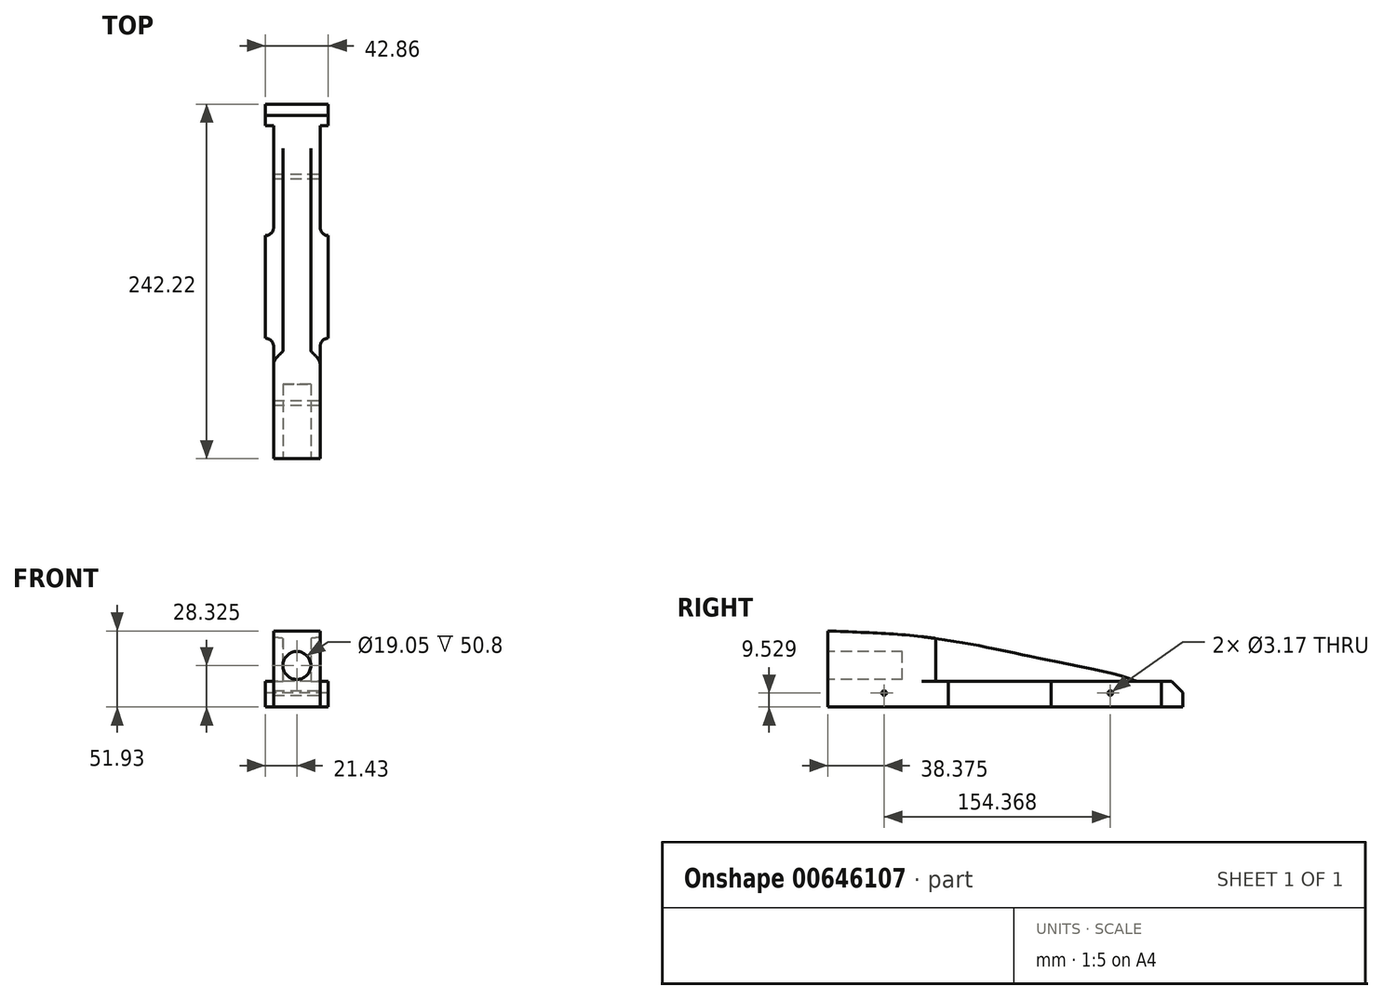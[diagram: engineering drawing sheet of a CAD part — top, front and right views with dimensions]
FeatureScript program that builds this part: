
annotation { "Feature Type Name" : "Feature", "Feature Type Description" : "" }
export const myFeature = defineFeature(function(context is Context, id is Id, definition is map)
    precondition{}
    {
        {
            var Q0;
            Q0=qCreatedBy(makeId("Right.planeOp"),FACE);
            var sketch = newSketch(context, id + "F0", { "sketchPlane" : qUnion([Q0])});
            skLineSegment(sketch, "E0", {"start": v(-152.4, 0) * mm, "end": v(152.4, 0) * mm});
            skLineSegment(sketch, "E1", {"start": v(-152.4, 0) * mm, "end": v(-152.4, 69.85) * mm});
            skLineSegment(sketch, "E2", {"start": v(152.4, 0) * mm, "end": v(152.4, 19.05) * mm});
            skLineSegment(sketch, "E3", {"start": v(152.4, 19.05) * mm, "end": v(-152.4, 69.85) * mm});
            skPoint(sketch, "E4.endSnap0", {"position": v(-152.4, 34.93) * mm});
            skLineSegment(sketch, "E5.0", {"start": v(-95.25, 50.8) * mm, "end": v(-152.4, 50.8) * mm, "construction": true});
            skLineSegment(sketch, "E5.1", {"start": v(-95.25, 50.8) * mm, "end": v(-95.25, 19.05) * mm, "construction": true});
            skLineSegment(sketch, "E5.2", {"start": v(-95.25, 19.05) * mm, "end": v(-152.4, 19.05) * mm, "construction": true});
            skSolve(sketch);
        }
        {
            var Q0;
            Q0=makeQuery(id+"F0.imprint","IMPRINT",FACE,{"disambiguationData":[TD([[makeQuery(id+"F0.imprint","IMPRINT",EDGE,{"derivedFrom":sQuery(id+"F0.wireOp",EDGE,"E0")}),1.0]])]});
            extrude(context, id + "F1", {"entities" : qUnion([Q0]), "depth" : 42.86 * mm, "symmetric" : true});
        }
        {
            var Q0;
            Q0=makeQuery(id+"F1.opExtrude","SWEPT_FACE",FACE,{"disambiguationData":[OSD([sQuery(id+"F0.wireOp",EDGE,"E1")])]});
            var sketch = newSketch(context, id + "F2", { "sketchPlane" : qUnion([Q0])});
            skLineSegment(sketch, "E6", {"start": v(21.43, 34.93) * mm, "end": v(0, 34.93) * mm, "construction": true});
            skCircle(sketch, "E7", {"center": v(0, 34.93) * mm, "radius": 9.53 * mm});
            skSolve(sketch);
        }
        {
            var Q0;
            Q0=makeQuery(id+"F2.imprint","IMPRINT",FACE,{"disambiguationData":[TD([[makeQuery(id+"F2.imprint","IMPRINT",EDGE,{"derivedFrom":sQuery(id+"F2.wireOp",EDGE,"E7")}),1.0]])]});
            var Q1;
            Q1=sQuery(id+"F2.wireOp",EDGE,"E7");
            extrude(context, id + "F3", {"entities" : qUnion([Q0]), "operationType" : NewBodyOperationType.REMOVE, "surfaceEntities" : qUnion([Q1]), "oppositeDirection" : true, "depth" : 50.8 * mm});
        }
        {
            var Q0;
            Q0=makeQuery(id+"F1.opExtrude","CAP_FACE",FACE,{"disambiguationData":[OSD([sQuery(id+"F0.wireOp",EDGE,"E0"),sQuery(id+"F0.wireOp",EDGE,"E1"),sQuery(id+"F0.wireOp",EDGE,"E2"),sQuery(id+"F0.wireOp",EDGE,"E3")])],"isStart":false});
            var sketch = newSketch(context, id + "F4", { "sketchPlane" : qUnion([Q0])});
            skLineSegment(sketch, "E8", {"start": v(-152.4, 34.93) * mm, "end": v(-152.4, 44.45) * mm, "construction": true});
            skLineSegment(sketch, "E9.0", {"start": v(-95.25, 19.05) * mm, "end": v(-152.4, 19.05) * mm, "construction": true});
            skLineSegment(sketch, "E9.1", {"start": v(-95.25, 50.8) * mm, "end": v(-95.25, 19.05) * mm, "construction": true});
            skLineSegment(sketch, "E9.2", {"start": v(-152.4, 50.8) * mm, "end": v(-95.25, 50.8) * mm, "construction": true});
            skLineSegment(sketch, "E10", {"start": v(-152.4, 44.45) * mm, "end": v(-101.6, 44.45) * mm, "construction": true});
            skLineSegment(sketch, "E11", {"start": v(-101.6, 44.45) * mm, "end": v(-101.6, 25.4) * mm, "construction": true});
            skLineSegment(sketch, "E12", {"start": v(-101.6, 25.4) * mm, "end": v(-152.4, 25.4) * mm, "construction": true});
            skFitSpline(sketch, "E13", {"points": [v(-152.4, 58.53) * mm, v(-91.68, 54.96) * mm, v(-40.9, 46.73) * mm, v(0, 38.24) * mm, v(57.15, 24.13) * mm], "startDerivative": vector(228.74, -10.44) * mm, "endDerivative": vector(48.82, -45.78) * mm});
            skLineSegment(sketch, "E14", {"start": v(57.15, 24.13) * mm, "end": v(57.15, 24.13) * mm});
            skLineSegment(sketch, "E15", {"start": v(-152.4, 50.8) * mm, "end": v(-152.4, 58.53) * mm});
            skPoint(sketch, "E16", {"position": v(0, 44.45) * mm});
            skLineSegment(sketch, "E17", {"start": v(57.15, 24.13) * mm, "end": v(166.37, 24.13) * mm});
            skLineSegment(sketch, "E18", {"start": v(166.37, 24.13) * mm, "end": v(-166.53, 95.56) * mm});
            skLineSegment(sketch, "E19", {"start": v(-166.53, 95.56) * mm, "end": v(-152.4, 58.53) * mm});
            skSolve(sketch);
        }
        {
            var Q0;
            Q0=makeQuery(id+"F1.opExtrude","SWEPT_FACE",FACE,{"disambiguationData":[OSD([sQuery(id+"F0.wireOp",EDGE,"E0")])]});
            var sketch = newSketch(context, id + "F5", { "sketchPlane" : qUnion([Q0])});
            skLineSegment(sketch, "E20", {"start": v(15.88, 152.4) * mm, "end": v(15.88, 95.25) * mm, "construction": true});
            skLineSegment(sketch, "E21", {"start": v(15.88, 95.25) * mm, "end": v(-15.87, 95.25) * mm, "construction": true});
            skLineSegment(sketch, "E22", {"start": v(-15.87, 95.25) * mm, "end": v(-15.87, 152.4) * mm, "construction": true});
            skLineSegment(sketch, "E23", {"start": v(0, 152.4) * mm, "end": v(-9.53, 152.4) * mm, "construction": true});
            skLineSegment(sketch, "E24", {"start": v(-9.53, 152.4) * mm, "end": v(-9.53, 101.6) * mm, "construction": true});
            skLineSegment(sketch, "E25", {"start": v(-9.52, 101.6) * mm, "end": v(9.53, 101.6) * mm, "construction": true});
            skLineSegment(sketch, "E26", {"start": v(9.53, 101.6) * mm, "end": v(9.53, 152.4) * mm, "construction": true});
            skLineSegment(sketch, "E27", {"start": v(15.88, 152.4) * mm, "end": v(15.88, 95.25) * mm});
            skLineSegment(sketch, "E28", {"start": v(-15.87, 95.25) * mm, "end": v(-15.87, 152.4) * mm});
            skLineSegment(sketch, "E29", {"start": v(15.88, 95.25) * mm, "end": v(15.88, 75.65) * mm});
            skLineSegment(sketch, "E30", {"start": v(-15.87, 95.25) * mm, "end": v(-15.87, 75.65) * mm});
            skLineSegment(sketch, "E31", {"start": v(-21.43, 70.1) * mm, "end": v(-21.43, 0) * mm});
            skLineSegment(sketch, "E32", {"start": v(21.43, 70.1) * mm, "end": v(21.43, 0) * mm});
            skLineSegment(sketch, "E33", {"start": v(21.43, 0) * mm, "end": v(21.43, -5.56) * mm});
            skArc(sketch, "E34", {"start": v(-21.43, 70.1) * mm, "mid": v(-17.5, 71.72) * mm, "end": v(-15.87, 75.65) * mm});
            skArc(sketch, "E35", {"start": v(15.88, 75.65) * mm, "mid": v(17.5, 71.72) * mm, "end": v(21.43, 70.1) * mm});
            skArc(sketch, "E36", {"start": v(21.43, 0) * mm, "mid": v(17.5, -1.63) * mm, "end": v(15.87, -5.56) * mm});
            skArc(sketch, "E37", {"start": v(-15.87, -5.56) * mm, "mid": v(-17.5, -1.63) * mm, "end": v(-21.43, 0) * mm});
            skLineSegment(sketch, "E38", {"start": v(-15.87, -5.56) * mm, "end": v(-15.87, -43.38) * mm});
            skLineSegment(sketch, "E39", {"start": v(15.87, -5.56) * mm, "end": v(15.87, -43.38) * mm});
            skLineSegment(sketch, "E40", {"start": v(15.87, -43.38) * mm, "end": v(15.87, -75.12) * mm});
            skLineSegment(sketch, "E41", {"start": v(-15.87, -43.38) * mm, "end": v(-15.87, -75.12) * mm});
            skLineSegment(sketch, "E42", {"start": v(-15.87, -75.12) * mm, "end": v(-21.43, -75.12) * mm});
            skLineSegment(sketch, "E43", {"start": v(-21.43, -75.12) * mm, "end": v(-21.43, -89.82) * mm});
            skLineSegment(sketch, "E44", {"start": v(-21.43, -89.82) * mm, "end": v(21.43, -89.82) * mm});
            skLineSegment(sketch, "E45", {"start": v(21.43, -89.82) * mm, "end": v(21.43, -75.12) * mm});
            skLineSegment(sketch, "E46", {"start": v(21.43, -75.12) * mm, "end": v(15.87, -75.12) * mm});
            skLineSegment(sketch, "E47", {"start": v(-21.43, -75.12) * mm, "end": v(-21.43, 0) * mm});
            skLineSegment(sketch, "E48", {"start": v(-21.43, 70.1) * mm, "end": v(-21.43, 152.4) * mm});
            skLineSegment(sketch, "E49", {"start": v(-21.7, 152.13) * mm, "end": v(-15.87, 152.4) * mm});
            skLineSegment(sketch, "E50", {"start": v(15.88, 152.4) * mm, "end": v(21.43, 152.4) * mm});
            skLineSegment(sketch, "E51", {"start": v(22.12, 152.57) * mm, "end": v(21.43, 70.1) * mm});
            skLineSegment(sketch, "E52", {"start": v(21.43, -75.12) * mm, "end": v(21.43, 0) * mm});
            skLineSegment(sketch, "E53", {"start": v(-21.43, -89.82) * mm, "end": v(-21.43, -152.4) * mm});
            skLineSegment(sketch, "E54", {"start": v(-21.43, -152.4) * mm, "end": v(21.43, -152.4) * mm});
            skLineSegment(sketch, "E55", {"start": v(21.43, -152.4) * mm, "end": v(21.43, -89.82) * mm});
            skSolve(sketch);
        }
        {
            var Q0;
            {var subQ0=sQuery(id+"F5.wireOp",EDGE,"E27");Q0=makeQuery(id+"F5.imprint","IMPRINT",FACE,{"disambiguationData":[TD([[makeQuery(id+"F5.imprint","IMPRINT",EDGE,{"derivedFrom":subQ0}),-1.0]])]});}
            var sketch = newSketch(context, id + "F6", { "sketchPlane" : qUnion([Q0])});
            skSolve(sketch);
        }
        {
            var Q0;
            Q0=qSketchRegion(id+"F5",true);
            var Q1;
            Q1=makeQuery(id+"F5.imprint","IMPRINT",FACE,{"disambiguationData":[TD([[makeQuery(id+"F5.imprint","IMPRINT",EDGE,{"derivedFrom":sQuery(id+"F5.wireOp",EDGE,"E27")}),1.0]])]});
            extrude(context, id + "F7", {"entities" : qUnion([Q0, Q1]), "operationType" : NewBodyOperationType.REMOVE, "oppositeDirection" : true, "depth" : 117.86 * mm});
        }
        {
            var Q0;
            {var subQ2=sQuery(id+"F0.wireOp",EDGE,"E1");Q0=makeQuery(id+"F7.boolean.opBoolean","SPLIT",FACE,{"disambiguationData":[TD([makeQuery(id+"F7.opExtrude","SWEPT_FACE",FACE,{"disambiguationData":[OSD([sQuery(id+"F5.wireOp",EDGE,"E49")])]})])],"derivedFrom":makeQuery(id+"F1.opExtrude","SWEPT_FACE",FACE,{"disambiguationData":[OSD([subQ2])]})});}
            var sketch = newSketch(context, id + "F8", { "sketchPlane" : qUnion([Q0])});
            skLineSegment(sketch, "E56.bottom", {"start": v(-21.43, 69.85) * mm, "end": v(-15.87, 69.85) * mm});
            skLineSegment(sketch, "E56.top", {"start": v(-21.43, 0) * mm, "end": v(-15.87, 0) * mm});
            skLineSegment(sketch, "E56.left", {"start": v(-21.43, 69.85) * mm, "end": v(-21.43, 0) * mm});
            skLineSegment(sketch, "E56.right", {"start": v(-15.87, 69.85) * mm, "end": v(-15.87, 0) * mm});
            skSolve(sketch);
        }
        {
            var Q0;
            Q0=qSketchRegion(id+"F8",true);
            extrude(context, id + "F9", {"entities" : qUnion([Q0]), "operationType" : NewBodyOperationType.REMOVE, "oppositeDirection" : true, "depth" : 25.4 * mm});
        }
        {
            var Q0;
            Q0=qSketchRegion(id+"F4",true);
            extrude(context, id + "F10", {"entities" : qUnion([Q0]), "operationType" : NewBodyOperationType.REMOVE, "oppositeDirection" : true, "depth" : 78.23 * mm});
        }
        {
            var Q0;
            Q0=makeQuery(id+"F10.boolean.opBoolean","COPY",FACE,{"derivedFrom":makeQuery(id+"F10.opExtrude","SWEPT_FACE",FACE,{"disambiguationData":[OSD([sQuery(id+"F4.wireOp",EDGE,"E17")])]})});
            var sketch = newSketch(context, id + "F11", { "sketchPlane" : qUnion([Q0])});
            skLineSegment(sketch, "E57", {"start": v(15.87, 75.12) * mm, "end": v(9.52, 75.12) * mm});
            skLineSegment(sketch, "E58", {"start": v(9.52, 75.12) * mm, "end": v(9.52, -78.86) * mm});
            skLineSegment(sketch, "E59", {"start": v(9.52, -78.86) * mm, "end": v(26.53, -78.86) * mm});
            skLineSegment(sketch, "E60", {"start": v(26.53, -78.86) * mm, "end": v(26.53, 75.12) * mm});
            skLineSegment(sketch, "E61", {"start": v(26.53, 75.12) * mm, "end": v(15.87, 75.12) * mm});
            skSolve(sketch);
        }
        {
            var Q0;
            Q0=qSketchRegion(id+"F11",true);
            extrude(context, id + "F12", {"entities" : qUnion([Q0]), "operationType" : NewBodyOperationType.REMOVE, "depth" : 65.8 * mm});
        }
        {
            var Q0;
            Q0=makeQuery(id+"F12.boolean.opBoolean","MERGE",FACE,{"derivedFrom":[makeQuery(id+"F10.boolean.opBoolean","COPY",FACE,{"derivedFrom":makeQuery(id+"F10.opExtrude","SWEPT_FACE",FACE,{"disambiguationData":[OSD([sQuery(id+"F4.wireOp",EDGE,"E17")])]})}),makeQuery(id+"F12.opExtrude","CAP_FACE",FACE,{"disambiguationData":[OSD([sQuery(id+"F11.wireOp",EDGE,"E57"),sQuery(id+"F11.wireOp",EDGE,"E58"),sQuery(id+"F11.wireOp",EDGE,"E59"),sQuery(id+"F11.wireOp",EDGE,"E60"),sQuery(id+"F11.wireOp",EDGE,"E61")])],"isStart":true})]});
            var sketch = newSketch(context, id + "F13", { "sketchPlane" : qUnion([Q0])});
            skLineSegment(sketch, "E62", {"start": v(-15.87, 57.15) * mm, "end": v(-9.52, 57.15) * mm});
            skLineSegment(sketch, "E63", {"start": v(-9.52, 57.15) * mm, "end": v(-9.52, -78.86) * mm});
            skLineSegment(sketch, "E64", {"start": v(-9.52, -78.86) * mm, "end": v(-37.05, -78.86) * mm});
            skLineSegment(sketch, "E65", {"start": v(-37.05, -78.86) * mm, "end": v(-28.36, 57.15) * mm});
            skLineSegment(sketch, "E66", {"start": v(-28.36, 57.15) * mm, "end": v(-15.87, 57.15) * mm});
            skSolve(sketch);
        }
        {
            var Q0;
            Q0=qSketchRegion(id+"F13",true);
            extrude(context, id + "F14", {"entities" : qUnion([Q0]), "operationType" : NewBodyOperationType.REMOVE, "depth" : 70.1 * mm});
        }
        {
            var Q0;
            {var subQ0=sQuery(id+"F5.wireOp",EDGE,"E27");Q0=makeQuery(id+"F6.imprint","IMPRINT",FACE,{"disambiguationData":[TD([[makeQuery(id+"F6.imprint","IMPRINT",EDGE,{"derivedFrom":makeQuery(id+"F5.imprint","IMPRINT",EDGE,{"derivedFrom":subQ0})}),-1.0]])]});}
            var sketch = newSketch(context, id + "F15", { "sketchPlane" : qUnion([Q0])});
            skLineSegment(sketch, "E67", {"start": v(-32.66, -99.62) * mm, "end": v(53.37, -99.62) * mm});
            skLineSegment(sketch, "E68", {"start": v(53.37, -100.92) * mm, "end": v(53.37, 166.9) * mm});
            skLineSegment(sketch, "E69", {"start": v(49.5, 166.9) * mm, "end": v(-47.54, 166.9) * mm});
            skLineSegment(sketch, "E70", {"start": v(-47.54, 164.31) * mm, "end": v(-32.66, -99.62) * mm});
            skSolve(sketch);
        }
        {
            var Q0;
            Q0=qSketchRegion(id+"F15",true);
            var Q1;
            {var subQ0=sQuery(id+"F5.wireOp",EDGE,"E27");Q1=makeQuery(id+"F6.imprint","IMPRINT",FACE,{"disambiguationData":[TD([[makeQuery(id+"F6.imprint","IMPRINT",EDGE,{"derivedFrom":makeQuery(id+"F5.imprint","IMPRINT",EDGE,{"derivedFrom":subQ0})}),-1.0]])]});}
            extrude(context, id + "F16", {"entities" : qUnion([Q0, Q1]), "operationType" : NewBodyOperationType.REMOVE, "oppositeDirection" : true, "depth" : 6.6 * mm});
        }
        {
            var Q0;
            Q0=makeQuery(id+"F10.boolean.opBoolean","INTERSECT",EDGE,{"derivedFrom":[makeQuery(id+"F7.boolean.opBoolean","COPY",FACE,{"derivedFrom":makeQuery(id+"F7.opExtrude","SWEPT_FACE",FACE,{"disambiguationData":[OSD([sQuery(id+"F5.wireOp",EDGE,"E44")])]})}),makeQuery(id+"F10.opExtrude","SWEPT_FACE",FACE,{"disambiguationData":[OSD([sQuery(id+"F4.wireOp",EDGE,"E17")])]})]});
            chamfer(context, id + "F17", {"entities" : qUnion([Q0]), "width" : 7.62 * mm, "tangentPropagation" : true});
        }
        {
            var Q0;
            Q0=makeQuery(id+"F16.boolean.opBoolean","COPY",EDGE,{"derivedFrom":makeQuery(id+"F16.opExtrude","CAP_EDGE",EDGE,{"disambiguationData":[OSD([sQuery(id+"F5.wireOp",EDGE,"E44")])],"isStart":false})});
            var Q1;
            Q1=makeQuery(id+"F10.boolean.opBoolean","COPY",EDGE,{"derivedFrom":makeQuery(id+"F10.opExtrude","SWEPT_EDGE",EDGE,{"disambiguationData":[OSD([sQuery(id+"F4.wireOp",EDGE,"E13"),sQuery(id+"F4.wireOp",EDGE,"E17")])]})});
            fillet(context, id + "F18", {"entities" : qUnion([Q0, Q1]), "radius" : 7.62 * mm, "tangentPropagation" : true, "allowEdgeOverflow" : false});
        }
        {
            var Q0;
            Q0=makeQuery(id+"F14.boolean.opBoolean","INTERSECT",EDGE,{"derivedFrom":[makeQuery(id+"F7.boolean.opBoolean","COPY",FACE,{"derivedFrom":makeQuery(id+"F7.opExtrude","SWEPT_FACE",FACE,{"disambiguationData":[OSD([sQuery(id+"F5.wireOp",EDGE,"E28"),sQuery(id+"F5.wireOp",EDGE,"E30")])]})}),makeQuery(id+"F14.opExtrude","SWEPT_FACE",FACE,{"disambiguationData":[OSD([sQuery(id+"F13.wireOp",EDGE,"E64")])]})]});
            var Q1;
            Q1=makeQuery(id+"F12.boolean.opBoolean","INTERSECT",EDGE,{"derivedFrom":[makeQuery(id+"F7.boolean.opBoolean","COPY",FACE,{"derivedFrom":makeQuery(id+"F7.opExtrude","SWEPT_FACE",FACE,{"disambiguationData":[OSD([sQuery(id+"F5.wireOp",EDGE,"E27"),sQuery(id+"F5.wireOp",EDGE,"E29")])]})}),makeQuery(id+"F12.opExtrude","SWEPT_FACE",FACE,{"disambiguationData":[OSD([sQuery(id+"F11.wireOp",EDGE,"E59")])]})]});
            chamfer(context, id + "F19", {"entities" : qUnion([Q0, Q1]), "width" : 6.35 * mm, "tangentPropagation" : true});
        }
        {
            var Q0;
            {var subQ0=makeQuery(id+"F7.boolean.opBoolean","COPY",FACE,{"derivedFrom":makeQuery(id+"F7.opExtrude","SWEPT_FACE",FACE,{"disambiguationData":[OSD([sQuery(id+"F5.wireOp",EDGE,"E28"),sQuery(id+"F5.wireOp",EDGE,"E30")])]})});Q0=makeQuery(id+"F19.opChamfer","BLEND_EDGE",EDGE,{"blendedFrom":[makeQuery(id+"F14.boolean.opBoolean","INTERSECT",EDGE,{"derivedFrom":[subQ0,makeQuery(id+"F14.opExtrude","SWEPT_FACE",FACE,{"disambiguationData":[OSD([sQuery(id+"F13.wireOp",EDGE,"E64")])]})]}),subQ0],"blendedInto":[subQ0]});}
            var Q1;
            {var subQ0=makeQuery(id+"F7.boolean.opBoolean","COPY",FACE,{"derivedFrom":makeQuery(id+"F7.opExtrude","SWEPT_FACE",FACE,{"disambiguationData":[OSD([sQuery(id+"F5.wireOp",EDGE,"E27"),sQuery(id+"F5.wireOp",EDGE,"E29")])]})});Q1=makeQuery(id+"F19.opChamfer","BLEND_EDGE",EDGE,{"blendedFrom":[makeQuery(id+"F12.boolean.opBoolean","INTERSECT",EDGE,{"derivedFrom":[subQ0,makeQuery(id+"F12.opExtrude","SWEPT_FACE",FACE,{"disambiguationData":[OSD([sQuery(id+"F11.wireOp",EDGE,"E59")])]})]}),subQ0],"blendedInto":[subQ0]});}
            fillet(context, id + "F20", {"entities" : qUnion([Q0, Q1]), "radius" : 7.62 * mm, "tangentPropagation" : true, "allowEdgeOverflow" : false});
        }
        {
            var Q0;
            Q0=makeQuery(id+"F7.boolean.opBoolean","COPY",FACE,{"derivedFrom":makeQuery(id+"F7.opExtrude","SWEPT_FACE",FACE,{"disambiguationData":[OSD([sQuery(id+"F5.wireOp",EDGE,"E27"),sQuery(id+"F5.wireOp",EDGE,"E29")])]})});
            var sketch = newSketch(context, id + "F21", { "sketchPlane" : qUnion([Q0])});
            skCircle(sketch, "E71", {"center": v(-114.03, 16.13) * mm, "radius": 1.59 * mm});
            skSolve(sketch);
        }
        {
            var Q0;
            Q0=qSketchRegion(id+"F21",true);
            extrude(context, id + "F22", {"entities" : qUnion([Q0]), "operationType" : NewBodyOperationType.REMOVE, "oppositeDirection" : true, "depth" : 32.26 * mm});
        }
        {
            var Q0;
            Q0=makeQuery(id+"F7.boolean.opBoolean","COPY",FACE,{"derivedFrom":makeQuery(id+"F7.opExtrude","SWEPT_FACE",FACE,{"disambiguationData":[OSD([sQuery(id+"F5.wireOp",EDGE,"E39"),sQuery(id+"F5.wireOp",EDGE,"E40")])]})});
            var sketch = newSketch(context, id + "F23", { "sketchPlane" : qUnion([Q0])});
            skCircle(sketch, "E72", {"center": v(40.34, 16.13) * mm, "radius": 1.59 * mm});
            skSolve(sketch);
        }
        {
            var Q0;
            Q0=qSketchRegion(id+"F23",true);
            extrude(context, id + "F24", {"entities" : qUnion([Q0]), "operationType" : NewBodyOperationType.REMOVE, "oppositeDirection" : true, "depth" : 36.07 * mm});
        }
    });
